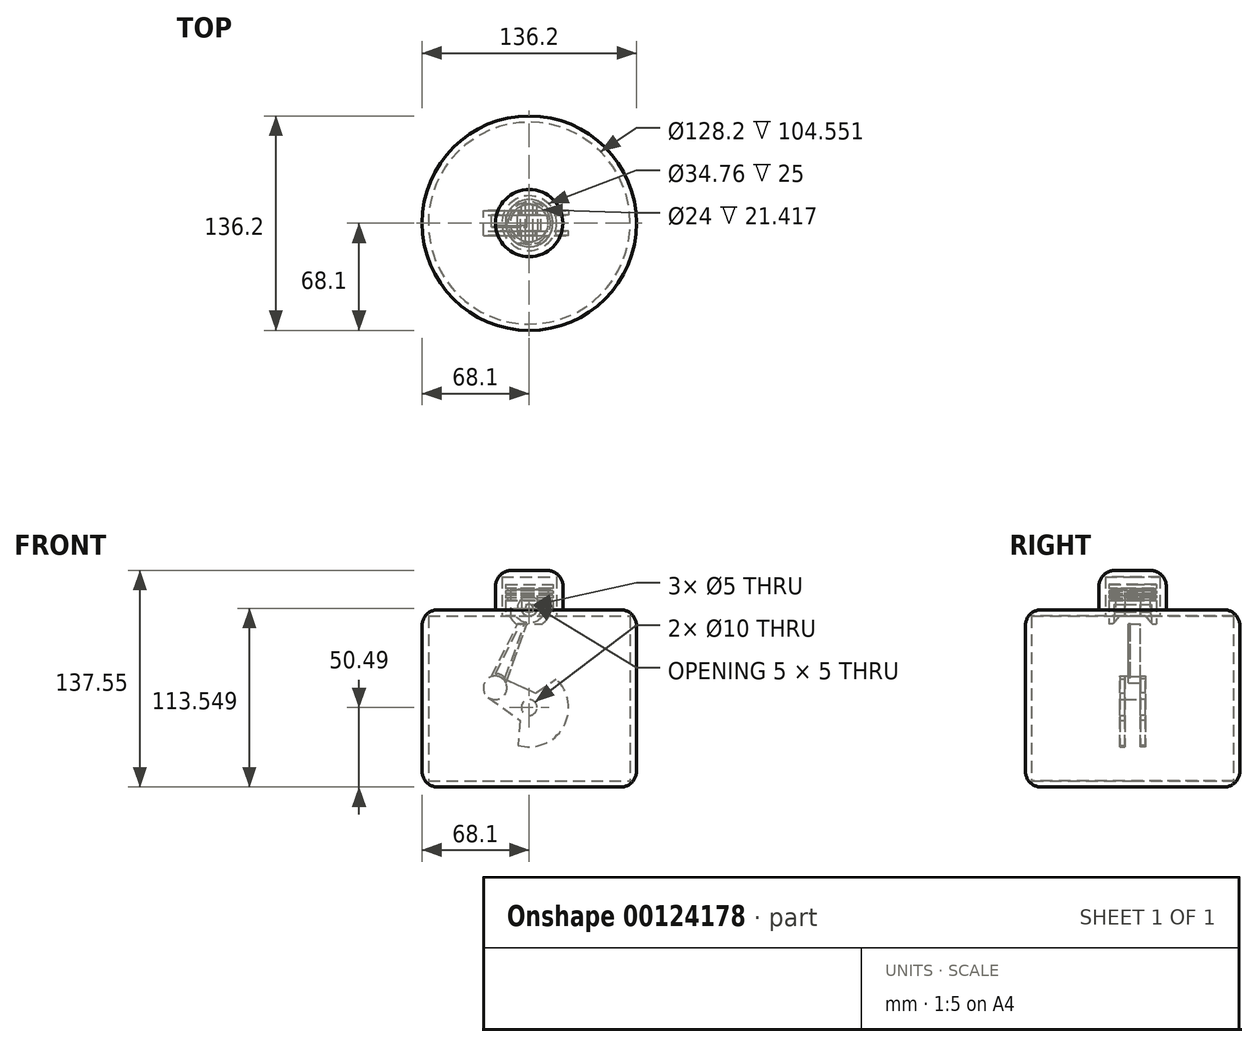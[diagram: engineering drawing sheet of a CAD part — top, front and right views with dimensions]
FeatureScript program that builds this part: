
annotation { "Feature Type Name" : "Feature", "Feature Type Description" : "" }
export const myFeature = defineFeature(function(context is Context, id is Id, definition is map)
    precondition{}
    {
        {
            var Q0;
            Q0=qCreatedBy(makeId("Front.planeOp"),FACE);
            var sketch = newSketch(context, id + "F0", { "sketchPlane" : qUnion([Q0])});
            skLineSegment(sketch, "E0", {"start": v(-42.81, 0) * mm, "end": v(53.39, 0) * mm, "construction": true});
            skLineSegment(sketch, "E1", {"start": v(-42.81, 50) * mm, "end": v(56.65, 50) * mm, "construction": true});
            skLineSegment(sketch, "E2", {"start": v(-46.8, 90) * mm, "end": v(65.37, 90) * mm, "construction": true});
            skLineSegment(sketch, "E3", {"start": v(0, 0) * mm, "end": v(0, 114.1) * mm, "construction": true});
            skLineSegment(sketch, "E4.bottom", {"start": v(15, 78.06) * mm, "end": v(-15, 78.06) * mm});
            skLineSegment(sketch, "E4.top", {"start": v(15, 53.06) * mm, "end": v(-15, 53.06) * mm});
            skLineSegment(sketch, "E4.left", {"start": v(15, 78.06) * mm, "end": v(15, 53.06) * mm});
            skLineSegment(sketch, "E4.right", {"start": v(-15, 78.06) * mm, "end": v(-15, 53.06) * mm});
            skPoint(sketch, "E4.middle", {"position": v(0, 65.56) * mm});
            skLineSegment(sketch, "E5.bottom", {"start": v(-5, 78.06) * mm, "end": v(5, 78.06) * mm});
            skLineSegment(sketch, "E5.top", {"start": v(-5, 71.06) * mm, "end": v(5, 71.06) * mm});
            skLineSegment(sketch, "E5.left", {"start": v(-5, 78.06) * mm, "end": v(-5, 71.06) * mm});
            skLineSegment(sketch, "E5.right", {"start": v(5, 78.06) * mm, "end": v(5, 71.06) * mm});
            skLineSegment(sketch, "E6", {"start": v(-5, 71.06) * mm, "end": v(-5, 63.06) * mm});
            skLineSegment(sketch, "E7", {"start": v(5, 71.06) * mm, "end": v(5, 63.06) * mm});
            skArc(sketch, "E8", {"start": v(-5, 63.06) * mm, "mid": v(0, 58.06) * mm, "end": v(5, 63.06) * mm});
            skCircle(sketch, "E9", {"center": v(0, 63.06) * mm, "radius": 2.5 * mm});
            skLineSegment(sketch, "E10", {"start": v(0, 63.06) * mm, "end": v(-21.65, 12.5) * mm});
            skLineSegment(sketch, "E11", {"start": v(-21.65, 12.5) * mm, "end": v(0, 0) * mm});
            skSolve(sketch);
        }
        {
            var Q0;
            Q0=qCreatedBy(makeId("Front.planeOp"),FACE);
            var sketch = newSketch(context, id + "F1", { "sketchPlane" : qUnion([Q0])});
            skLineSegment(sketch, "E12.0", {"start": v(15, 78.06) * mm, "end": v(0, 78.06) * mm});
            skLineSegment(sketch, "E12.1", {"start": v(15, 78.06) * mm, "end": v(15, 53.06) * mm});
            skLineSegment(sketch, "E12.2", {"start": v(15, 53.06) * mm, "end": v(0, 53.06) * mm});
            skLineSegment(sketch, "E13", {"start": v(0, 78.06) * mm, "end": v(0, 53.06) * mm});
            skPoint(sketch, "E14.orphan", {"position": v(-15, 53.06) * mm});
            skPoint(sketch, "E15.orphan", {"position": v(-15, 78.06) * mm});
            skSolve(sketch);
        }
        {
            var Q0;
            Q0 = qSketchRegion(id + "F1", true);
            var Q1;
            Q1=sQuery(id+"F0.wireOp",EDGE,"E3");
            revolve(context, id + "F2", {"entities" : qUnion([Q0]), "axis" : qUnion([Q1]), "revolveType" : RevolveType.FULL});
        }
        {
            var Q0;
            Q0=makeQuery(id+"F2.opRevolve","SWEPT_FACE",FACE,{"disambiguationData":[OSD([sQuery(id+"F1.wireOp",EDGE,"E12.2")])]});
            shell(context, id + "F3", {"entities" : qUnion([Q0]), "thickness" : 3 * mm});
        }
        {
            var Q0;
            Q0=makeQuery(id+"F0.imprint","IMPRINT",FACE,{"disambiguationData":[TD([[makeQuery(id+"F0.imprint","IMPRINT",EDGE,{"derivedFrom":sQuery(id+"F0.wireOp",EDGE,"E5.top")}),-1.0]])]});
            var Q1;
            Q1=makeQuery(id+"F0.imprint","IMPRINT",FACE,{"disambiguationData":[TD([[makeQuery(id+"F0.imprint","IMPRINT",EDGE,{"derivedFrom":sQuery(id+"F0.wireOp",EDGE,"E5.bottom")}),-1.0]])]});
            var Q2;
            Q2=makeQuery(id+"F3.opShell","OFFSET_FACE",FACE,{"disambiguationData":[OSD([sQuery(id+"F1.wireOp",EDGE,"E12.1")])]});
            var Q3;
            Q3=makeQuery(id+"F3.opShell","OFFSET_FACE",FACE,{"disambiguationData":[OSD([sQuery(id+"F1.wireOp",EDGE,"E12.1")])]});
            extrude(context, id + "F4", {"entities" : qUnion([Q0, Q1]), "operationType" : NewBodyOperationType.ADD, "endBound" : BoundingType.UP_TO_SURFACE, "endBoundEntityFace" : qUnion([Q2]), "depth" : 25 * mm, "hasSecondDirection" : true, "secondDirectionBound" : SecondDirectionBoundingType.UP_TO_SURFACE, "secondDirectionOppositeDirection" : true, "secondDirectionBoundEntityFace" : qUnion([Q3]), "secondDirectionDepth" : 25 * mm});
        }
        {
            var Q0;
            Q0=makeQuery(id+"F0.imprint","IMPRINT",FACE,{"disambiguationData":[TD([[makeQuery(id+"F0.imprint","IMPRINT",EDGE,{"derivedFrom":sQuery(id+"F0.wireOp",EDGE,"E5.top")}),-1.0]])]});
            extrude(context, id + "F5", {"entities" : qUnion([Q0]), "operationType" : NewBodyOperationType.REMOVE, "endBound" : BoundingType.SYMMETRIC, "oppositeDirection" : true, "depth" : 10 * mm});
        }
        {
            var Q0;
            Q0=qCreatedBy(makeId("Front.planeOp"),FACE);
            var sketch = newSketch(context, id + "F6", { "sketchPlane" : qUnion([Q0])});
            skCircle(sketch, "E16.0", {"center": v(0, 63.06) * mm, "radius": 2.5 * mm});
            skCircle(sketch, "E17", {"center": v(0, 63.06) * mm, "radius": 7.5 * mm});
            skCircle(sketch, "E18", {"center": v(-21.65, 12.5) * mm, "radius": 4 * mm});
            skCircle(sketch, "E19", {"center": v(-21.65, 12.5) * mm, "radius": 7.5 * mm});
            skLineSegment(sketch, "E20", {"start": v(-24.05, 19.6) * mm, "end": v(-5.08, 57.54) * mm});
            skLineSegment(sketch, "E21.MirrorCS", {"start": v(-14.85, 15.67) * mm, "end": v(-0.49, 55.58) * mm});
            skSolve(sketch);
        }
        {
            var Q0;
            Q0 = qSketchRegion(id + "F6", true);
            var Q1;
            Q1=makeQuery(id+"F5.boolean.opBoolean","COPY",FACE,{"derivedFrom":makeQuery(id+"F5.opExtrude","CAP_FACE",FACE,{"disambiguationData":[OSD([sQuery(id+"F0.wireOp",EDGE,"E5.top"),sQuery(id+"F0.wireOp",EDGE,"E6"),sQuery(id+"F0.wireOp",EDGE,"E7"),sQuery(id+"F0.wireOp",EDGE,"E8"),sQuery(id+"F0.wireOp",EDGE,"E9")])],"isStart":true})});
            var Q2;
            Q2=makeQuery(id+"F5.boolean.opBoolean","COPY",FACE,{"derivedFrom":makeQuery(id+"F5.opExtrude","CAP_FACE",FACE,{"disambiguationData":[OSD([sQuery(id+"F0.wireOp",EDGE,"E5.top"),sQuery(id+"F0.wireOp",EDGE,"E6"),sQuery(id+"F0.wireOp",EDGE,"E7"),sQuery(id+"F0.wireOp",EDGE,"E8"),sQuery(id+"F0.wireOp",EDGE,"E9")])],"isStart":false})});
            extrude(context, id + "F7", {"entities" : qUnion([Q0]), "endBound" : BoundingType.UP_TO_SURFACE, "endBoundEntityFace" : qUnion([Q1]), "depth" : 25 * mm, "hasSecondDirection" : true, "secondDirectionBound" : SecondDirectionBoundingType.UP_TO_SURFACE, "secondDirectionOppositeDirection" : true, "secondDirectionBoundEntityFace" : qUnion([Q2]), "secondDirectionDepth" : 25 * mm});
        }
        {
            var Q0;
            Q0=makeQuery(id+"F7.opExtrude","CAP_FACE",FACE,{"disambiguationData":[OSD([sQuery(id+"F6.wireOp",EDGE,"E16.0"),sQuery(id+"F6.wireOp",EDGE,"E17"),sQuery(id+"F6.wireOp",EDGE,"E18"),sQuery(id+"F6.wireOp",EDGE,"E19"),sQuery(id+"F6.wireOp",EDGE,"E20"),sQuery(id+"F6.wireOp",EDGE,"E21.MirrorCS")])],"isStart":false});
            var sketch = newSketch(context, id + "F8", { "sketchPlane" : qUnion([Q0])});
            skArc(sketch, "E22", {"start": v(-14.85, 15.67) * mm, "mid": v(-18.7, 19.4) * mm, "end": v(-24.05, 19.6) * mm});
            skArc(sketch, "E23", {"start": v(-5.08, 57.54) * mm, "mid": v(-2.95, 56.16) * mm, "end": v(-0.49, 55.58) * mm});
            skLineSegment(sketch, "E24.0", {"start": v(-24.05, 19.6) * mm, "end": v(-5.08, 57.54) * mm});
            skLineSegment(sketch, "E24.1", {"start": v(-14.85, 15.67) * mm, "end": v(-0.49, 55.58) * mm});
            skSolve(sketch);
        }
        {
            var Q0;
            Q0 = qSketchRegion(id + "F8", true);
            extrude(context, id + "F9", {"entities" : qUnion([Q0]), "operationType" : NewBodyOperationType.REMOVE, "oppositeDirection" : true, "depth" : 2.5 * mm});
        }
        {
            var Q0;
            Q0=makeQuery(id+"F9.boolean.opBoolean","COPY",FACE,{"derivedFrom":makeQuery(id+"F9.opExtrude","CAP_FACE",FACE,{"disambiguationData":[OSD([sQuery(id+"F8.wireOp",EDGE,"E22"),sQuery(id+"F8.wireOp",EDGE,"E23"),sQuery(id+"F8.wireOp",EDGE,"E24.0"),sQuery(id+"F8.wireOp",EDGE,"E24.1")])],"isStart":false})});
            var sketch = newSketch(context, id + "F10", { "sketchPlane" : qUnion([Q0])});
            skArc(sketch, "E25.0", {"start": v(-14.85, 15.67) * mm, "mid": v(-18.7, 19.4) * mm, "end": v(-24.05, 19.6) * mm, "construction": true});
            skLineSegment(sketch, "E25.1", {"start": v(-14.85, 15.67) * mm, "end": v(-0.49, 55.58) * mm, "construction": true});
            skLineSegment(sketch, "E25.2", {"start": v(-24.05, 19.6) * mm, "end": v(-5.08, 57.54) * mm, "construction": true});
            skArc(sketch, "E25.3", {"start": v(-5.08, 57.54) * mm, "mid": v(-2.95, 56.16) * mm, "end": v(-0.49, 55.58) * mm, "construction": true});
            skArc(sketch, "E26.0", {"start": v(-4.53, 55.28) * mm, "mid": v(-3.54, 54.79) * mm, "end": v(-2.5, 54.41) * mm});
            skLineSegment(sketch, "E26.1", {"start": v(-21.42, 21.5) * mm, "end": v(-4.53, 55.28) * mm});
            skArc(sketch, "E26.2", {"start": v(-15.3, 18.87) * mm, "mid": v(-18.1, 20.77) * mm, "end": v(-21.42, 21.5) * mm});
            skLineSegment(sketch, "E26.3", {"start": v(-15.3, 18.87) * mm, "end": v(-2.5, 54.41) * mm});
            skSolve(sketch);
        }
        {
            var Q0;
            Q0 = qSketchRegion(id + "F10", true);
            extrude(context, id + "F11", {"entities" : qUnion([Q0]), "operationType" : NewBodyOperationType.REMOVE, "oppositeDirection" : true, "depth" : 1 * mm});
        }
        {
            var Q0;
            {var subQ0=sQuery(id+"F6.wireOp",EDGE,"E18");var subQ1=sQuery(id+"F6.wireOp",EDGE,"E19");Q0=makeQuery(id+"F9.boolean.opBoolean","SPLIT",FACE,{"disambiguationData":[TD([makeQuery(id+"F7.opExtrude","SWEPT_FACE",FACE,{"disambiguationData":[OSD([subQ0])]})])],"derivedFrom":makeQuery(id+"F7.opExtrude","CAP_FACE",FACE,{"disambiguationData":[OSD([sQuery(id+"F6.wireOp",EDGE,"E16.0"),sQuery(id+"F6.wireOp",EDGE,"E17"),subQ0,subQ1,sQuery(id+"F6.wireOp",EDGE,"E20"),sQuery(id+"F6.wireOp",EDGE,"E21.MirrorCS")])],"isStart":false})});}
            var sketch = newSketch(context, id + "F12", { "sketchPlane" : qUnion([Q0])});
            skCircle(sketch, "E27.1", {"center": v(-21.65, 12.5) * mm, "radius": 7.5 * mm});
            skCircle(sketch, "E28", {"center": v(0, 0) * mm, "radius": 10 * mm});
            skLineSegment(sketch, "E29", {"start": v(-18.57, 19.34) * mm, "end": v(4.1, 9.12) * mm});
            skLineSegment(sketch, "E30", {"start": v(-26.03, 6.41) * mm, "end": v(-5.84, -8.12) * mm});
            skLineSegment(sketch, "E31", {"start": v(0, 0) * mm, "end": v(4.1, 9.12) * mm, "construction": true});
            skLineSegment(sketch, "E32", {"start": v(0, 0) * mm, "end": v(-5.84, -8.12) * mm, "construction": true});
            skCircle(sketch, "E33", {"center": v(0, 0) * mm, "radius": 5 * mm});
            skArc(sketch, "E34", {"start": v(-7.22, -23.93) * mm, "mid": v(21.65, -12.5) * mm, "end": v(17.11, 18.22) * mm});
            skLineSegment(sketch, "E35", {"start": v(4.1, 9.12) * mm, "end": v(17.11, 18.22) * mm});
            skLineSegment(sketch, "E36", {"start": v(-5.84, -8.12) * mm, "end": v(-7.22, -23.93) * mm});
            skLineSegment(sketch, "E37", {"start": v(-21.65, 12.5) * mm, "end": v(21.65, -12.5) * mm, "construction": true});
            skCircle(sketch, "E38.0", {"center": v(-21.65, 12.5) * mm, "radius": 4 * mm});
            skSolve(sketch);
        }
        {
            var Q0;
            Q0 = qSketchRegion(id + "F12", true);
            extrude(context, id + "F13", {"entities" : qUnion([Q0]), "depth" : 3 * mm});
        }
        {
            var Q0;
            Q0=makeQuery(id+"F13.opExtrude","SWEPT_BODY",BODY,{"disambiguationData":[OSD([sQuery(id+"F12.wireOp",EDGE,"E27.1"),sQuery(id+"F12.wireOp",EDGE,"E29"),sQuery(id+"F12.wireOp",EDGE,"E30"),sQuery(id+"F12.wireOp",EDGE,"E33"),sQuery(id+"F12.wireOp",EDGE,"E34"),sQuery(id+"F12.wireOp",EDGE,"E35"),sQuery(id+"F12.wireOp",EDGE,"E36")])]});
            var Q1;
            Q1=qCreatedBy(makeId("Front.planeOp"),FACE);
            mirror(context, id + "F14", {"entities" : qUnion([Q0]), "mirrorPlane" : qUnion([Q1])});
        }
        {
            var Q0;
            Q0=makeQuery(id+"F13.opExtrude","CAP_FACE",FACE,{"disambiguationData":[OSD([sQuery(id+"F12.wireOp",EDGE,"E27.1"),sQuery(id+"F12.wireOp",EDGE,"E29"),sQuery(id+"F12.wireOp",EDGE,"E30"),sQuery(id+"F12.wireOp",EDGE,"E33"),sQuery(id+"F12.wireOp",EDGE,"E34"),sQuery(id+"F12.wireOp",EDGE,"E35"),sQuery(id+"F12.wireOp",EDGE,"E36"),sQuery(id+"F12.wireOp",EDGE,"E38.0")])],"isStart":false});
            var sketch = newSketch(context, id + "F15", { "sketchPlane" : qUnion([Q0])});
            skCircle(sketch, "E39.0", {"center": v(-21.65, 12.5) * mm, "radius": 4 * mm});
            skSolve(sketch);
        }
        {
            var Q0;
            Q0 = qSketchRegion(id + "F15", true);
            var Q1;
            Q1=makeQuery(id+"F14.opPattern","COPY",FACE,{"derivedFrom":makeQuery(id+"F13.opExtrude","CAP_FACE",FACE,{"disambiguationData":[OSD([sQuery(id+"F12.wireOp",EDGE,"E27.1"),sQuery(id+"F12.wireOp",EDGE,"E29"),sQuery(id+"F12.wireOp",EDGE,"E30"),sQuery(id+"F12.wireOp",EDGE,"E33"),sQuery(id+"F12.wireOp",EDGE,"E34"),sQuery(id+"F12.wireOp",EDGE,"E35"),sQuery(id+"F12.wireOp",EDGE,"E36"),sQuery(id+"F12.wireOp",EDGE,"E38.0")])],"isStart":false}),"instanceName":"1"});
            extrude(context, id + "F16", {"entities" : qUnion([Q0]), "operationType" : NewBodyOperationType.ADD, "endBound" : BoundingType.UP_TO_SURFACE, "oppositeDirection" : true, "endBoundEntityFace" : qUnion([Q1]), "depth" : 25 * mm});
        }
        {
            var Q0;
            Q0=qCreatedBy(makeId("Right.planeOp"),FACE);
            var sketch = newSketch(context, id + "F17", { "sketchPlane" : qUnion([Q0])});
            skLineSegment(sketch, "E40", {"start": v(-12.5, 53.06) * mm, "end": v(-8.3, 58.06) * mm});
            skLineSegment(sketch, "E41", {"start": v(-8.3, 58.06) * mm, "end": v(8.3, 58.06) * mm});
            skLineSegment(sketch, "E42", {"start": v(8.3, 58.06) * mm, "end": v(12.5, 53.06) * mm});
            skLineSegment(sketch, "E43", {"start": v(12.5, 53.06) * mm, "end": v(-12.5, 53.06) * mm});
            skSolve(sketch);
        }
        {
            var Q0;
            Q0 = qSketchRegion(id + "F17", true);
            extrude(context, id + "F18", {"entities" : qUnion([Q0]), "operationType" : NewBodyOperationType.REMOVE, "endBound" : BoundingType.THROUGH_ALL, "oppositeDirection" : true, "depth" : 25 * mm, "hasSecondDirection" : true, "secondDirectionBound" : SecondDirectionBoundingType.THROUGH_ALL, "secondDirectionOppositeDirection" : false, "secondDirectionDepth" : 25 * mm});
        }
        {
            var Q0;
            Q0=qCreatedBy(makeId("Front.planeOp"),FACE);
            var sketch = newSketch(context, id + "F19", { "sketchPlane" : qUnion([Q0])});
            skLineSegment(sketch, "E44.0", {"start": v(-15, 75.56) * mm, "end": v(-15, 74.06) * mm});
            skLineSegment(sketch, "E45", {"start": v(-15, 75.56) * mm, "end": v(-13.5, 75.56) * mm});
            skLineSegment(sketch, "E46", {"start": v(-13.5, 75.56) * mm, "end": v(-13.5, 74.06) * mm});
            skLineSegment(sketch, "E47", {"start": v(-13.5, 74.06) * mm, "end": v(-15, 74.06) * mm});
            skLineSegment(sketch, "E48", {"start": v(-15, 72.56) * mm, "end": v(-13.5, 72.56) * mm});
            skLineSegment(sketch, "E49", {"start": v(-13.5, 72.56) * mm, "end": v(-13.5, 71.06) * mm});
            skLineSegment(sketch, "E50", {"start": v(-13.5, 71.06) * mm, "end": v(-15, 71.06) * mm});
            skLineSegment(sketch, "E51", {"start": v(-15, 69.56) * mm, "end": v(-13.5, 69.56) * mm});
            skLineSegment(sketch, "E52", {"start": v(-13.5, 69.56) * mm, "end": v(-13.5, 68.06) * mm});
            skLineSegment(sketch, "E53", {"start": v(-13.5, 68.06) * mm, "end": v(-15, 68.06) * mm});
            skPoint(sketch, "E44.2.end.orphan", {"position": v(15, 53.06) * mm});
            skPoint(sketch, "E44.2.start.orphan", {"position": v(15, 78.06) * mm});
            skPoint(sketch, "E44.3.end.orphan", {"position": v(-15, 78.06) * mm});
            skPoint(sketch, "E54.start.orphan", {"position": v(0, 78.06) * mm});
            skPoint(sketch, "E44.1.end.orphan", {"position": v(-15, 53.06) * mm});
            skPoint(sketch, "E44.1.start.orphan", {"position": v(0, 53.06) * mm});
            skLineSegment(sketch, "E55.trimOffspring", {"start": v(-15, 69.56) * mm, "end": v(-15, 68.06) * mm});
            skLineSegment(sketch, "E56.trimOffspring", {"start": v(-15, 72.56) * mm, "end": v(-15, 71.06) * mm});
            skSolve(sketch);
        }
        {
            var Q0;
            Q0 = qSketchRegion(id + "F19", true);
            var Q1;
            Q1=sQuery(id+"F0.wireOp",EDGE,"E3");
            revolve(context, id + "F20", {"operationType" : NewBodyOperationType.REMOVE, "entities" : qUnion([Q0]), "axis" : qUnion([Q1]), "revolveType" : RevolveType.FULL, "oppositeDirection" : true});
        }
        {
            var Q0;
            Q0=qCreatedBy(makeId("Front.planeOp"),FACE);
            var sketch = newSketch(context, id + "F21", { "sketchPlane" : qUnion([Q0])});
            skLineSegment(sketch, "E57", {"start": v(0, 87.06) * mm, "end": v(-21.38, 87.06) * mm});
            skLineSegment(sketch, "E58", {"start": v(-21.38, 87.06) * mm, "end": v(-21.38, 62.06) * mm});
            skLineSegment(sketch, "E59", {"start": v(-21.38, 62.06) * mm, "end": v(-68.1, 62.06) * mm});
            skLineSegment(sketch, "E60", {"start": v(-68.1, 62.06) * mm, "end": v(-68.1, -50.5) * mm});
            skLineSegment(sketch, "E61", {"start": v(-68.1, -50.5) * mm, "end": v(0, -50.5) * mm});
            skLineSegment(sketch, "E62", {"start": v(0, -50.5) * mm, "end": v(0, -46.5) * mm});
            skLineSegment(sketch, "E63.0", {"start": v(-64.1, -46.5) * mm, "end": v(0, -46.5) * mm});
            skLineSegment(sketch, "E63.1", {"start": v(0, 83.06) * mm, "end": v(-17.38, 83.06) * mm});
            skLineSegment(sketch, "E63.2", {"start": v(-17.38, 83.06) * mm, "end": v(-17.38, 58.06) * mm});
            skLineSegment(sketch, "E63.3", {"start": v(-17.38, 58.06) * mm, "end": v(-64.1, 58.06) * mm});
            skLineSegment(sketch, "E63.4", {"start": v(-64.1, 58.06) * mm, "end": v(-64.1, -46.5) * mm});
            skLineSegment(sketch, "E64", {"start": v(0, 83.06) * mm, "end": v(0, 87.06) * mm});
            skSolve(sketch);
        }
        {
            var Q0;
            Q0 = qSketchRegion(id + "F21", true);
            var Q1;
            Q1=sQuery(id+"F0.wireOp",EDGE,"E3");
            revolve(context, id + "F22", {"entities" : qUnion([Q0]), "axis" : qUnion([Q1]), "revolveType" : RevolveType.FULL});
        }
        {
            var Q0;
            Q0=makeQuery(id+"F22.opRevolve","SWEPT_EDGE",EDGE,{"disambiguationData":[OSD([sQuery(id+"F21.wireOp",EDGE,"E59"),sQuery(id+"F21.wireOp",EDGE,"E60")])]});
            var Q1;
            Q1=makeQuery(id+"F22.opRevolve","SWEPT_EDGE",EDGE,{"disambiguationData":[OSD([sQuery(id+"F21.wireOp",EDGE,"E57"),sQuery(id+"F21.wireOp",EDGE,"E58")])]});
            var Q2;
            Q2=makeQuery(id+"F22.opRevolve","SWEPT_FACE",FACE,{"disambiguationData":[OSD([sQuery(id+"F21.wireOp",EDGE,"E61")])]});
            fillet(context, id + "F23", {"entities" : qUnion([Q0, Q1, Q2]), "radius" : 10 * mm, "tangentPropagation" : true, "allowEdgeOverflow" : false});
        }
    });
